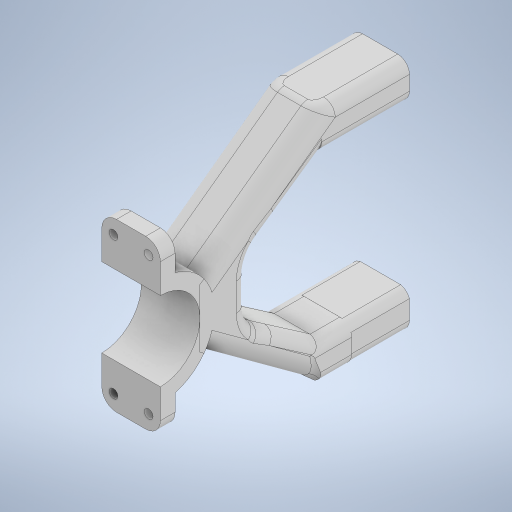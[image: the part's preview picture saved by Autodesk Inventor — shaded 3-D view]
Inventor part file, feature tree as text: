
AUTODESK INVENTOR PART (.ipt)
format: ipt  version: 2024.1 (Build 281209000, 209)  size: 570,880 bytes
history: native  units: mm
features: extrude x6, sketch x6, fillet x4, other x1
ambient origin geometry x8: Origin, YZ Plane, XZ Plane, XY Plane, X Axis, Y Axis, Z Axis, Center Point
bodies: Body1 (feature_tree), Body2 (feature_tree)
feature tree (17):
  other  "Sólido1"
  extrude  "Extrusão1"  Depth=6.5mm
  extrude  "Extrusão2"  Depth=4.0mm
  extrude  "Extrusão3"  Depth=3.0mm
  extrude  "Extrusão4"  Depth=4.0mm
  extrude  "Extrusão5"  Depth=3.0mm
  extrude  "Extrusão6"  Depth=4.0mm TaperAngle=0.0deg
  fillet  "Arredondamento1"  Radius=10.0mm
  fillet  "Arredondamento2"  Radius=2.0mm
  fillet  "Arredondamento3"  Radius=10.0mm
  fillet  "Arredondamento4"  Radius=20.0mm
  sketch  "Esboço1"  dims[d0=20.0mm d1=0.0mm d2=6.5mm]
  sketch  "Esboço2"  dims[d3=4.0mm d4=12.0mm]
  sketch  "Esboço3"  dims[d5=3.0mm d6=3.0mm]
  sketch  "Esboço4"  dims[d7=6.5mm d8=4.0mm]
  sketch  "Esboço5"  dims[d9=12.0mm d10=3.0mm]
  sketch  "Esboço6"  dims[d11=3.0mm d12=30.0mm d13=0.0mm d14=10.0mm d15=0.0mm d16=2.0mm d17=10.0mm d18=20.0mm d19=0.0mm d21=13.5mm d22=5.0mm d23=10.0mm d24=5.0mm d25=5.0mm d26=15.0mm d27=5.0mm d28=5.0mm d29=20.0mm d30=0.0mm d31=5.0mm d32=4.0mm d33=12.0mm d34=3.0mm d35=3.0mm d36=5.0mm d37=1.0mm d38=3.0mm d39=12.0mm d40=3.0mm d41=3.0mm d42=10.0mm d43=0.0mm d44=5.0mm d45=6.0mm d46=4.0mm d47=4.0mm d48=0.0mm d49=0.0mm]
